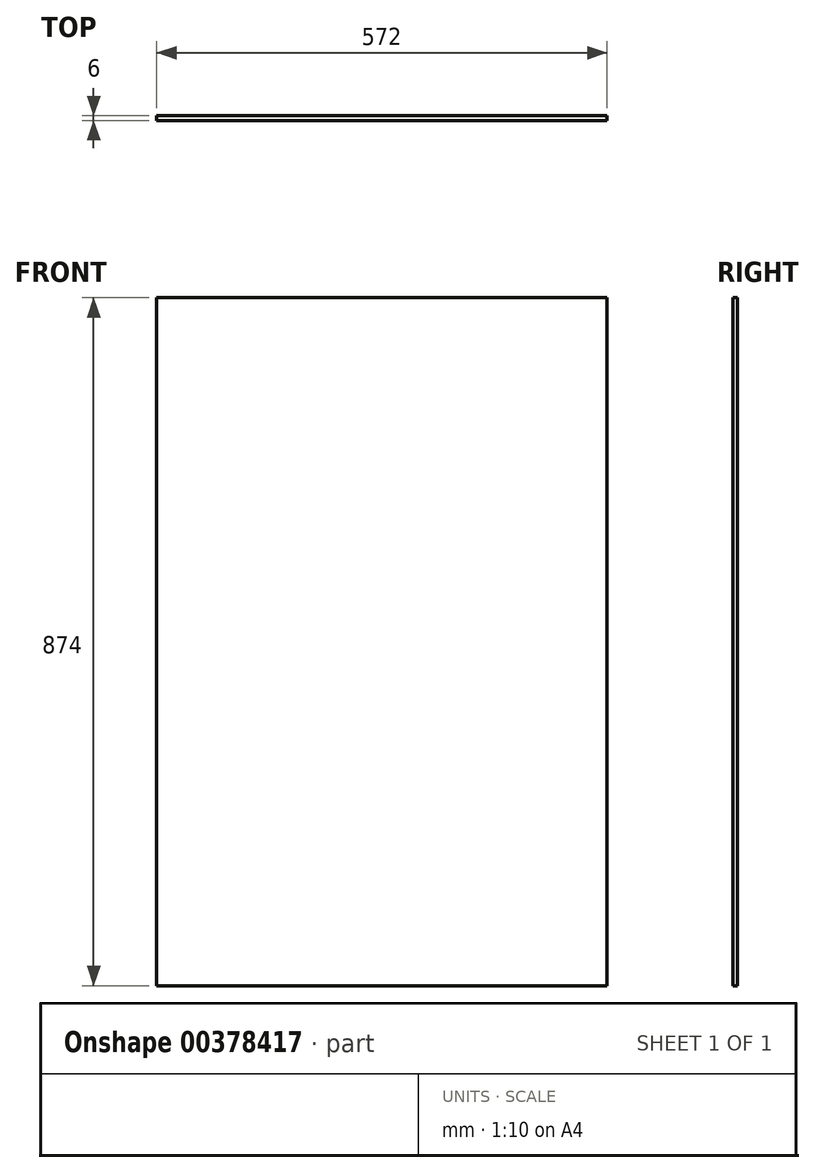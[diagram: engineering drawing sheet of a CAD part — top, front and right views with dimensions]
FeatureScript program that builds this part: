
annotation { "Feature Type Name" : "Feature", "Feature Type Description" : "" }
export const myFeature = defineFeature(function(context is Context, id is Id, definition is map)
    precondition{}
    {
        {
            var Q0;
            Q0=qCreatedBy(makeId("Front.planeOp"),FACE);
            var sketch = newSketch(context, id + "F0", { "sketchPlane" : qUnion([Q0])});
            skLineSegment(sketch, "E0.bottom", {"start": v(286, 437) * mm, "end": v(-286, 437) * mm});
            skLineSegment(sketch, "E0.top", {"start": v(286, -437) * mm, "end": v(-286, -437) * mm});
            skLineSegment(sketch, "E0.left", {"start": v(286, 437) * mm, "end": v(286, -437) * mm});
            skLineSegment(sketch, "E0.right", {"start": v(-286, 437) * mm, "end": v(-286, -437) * mm});
            skPoint(sketch, "E0.middle", {"position": v(0, 0) * mm});
            skSolve(sketch);
        }
        {
            var Q0;
            Q0=makeQuery(id+"F0.imprint","IMPRINT",FACE,{"disambiguationData":[TD([[makeQuery(id+"F0.imprint","IMPRINT",EDGE,{"derivedFrom":sQuery(id+"F0.wireOp",EDGE,"E0.bottom")}),1.0]])]});
            extrude(context, id + "F1", {"entities" : qUnion([Q0]), "depth" : 6 * mm});
        }
    });
